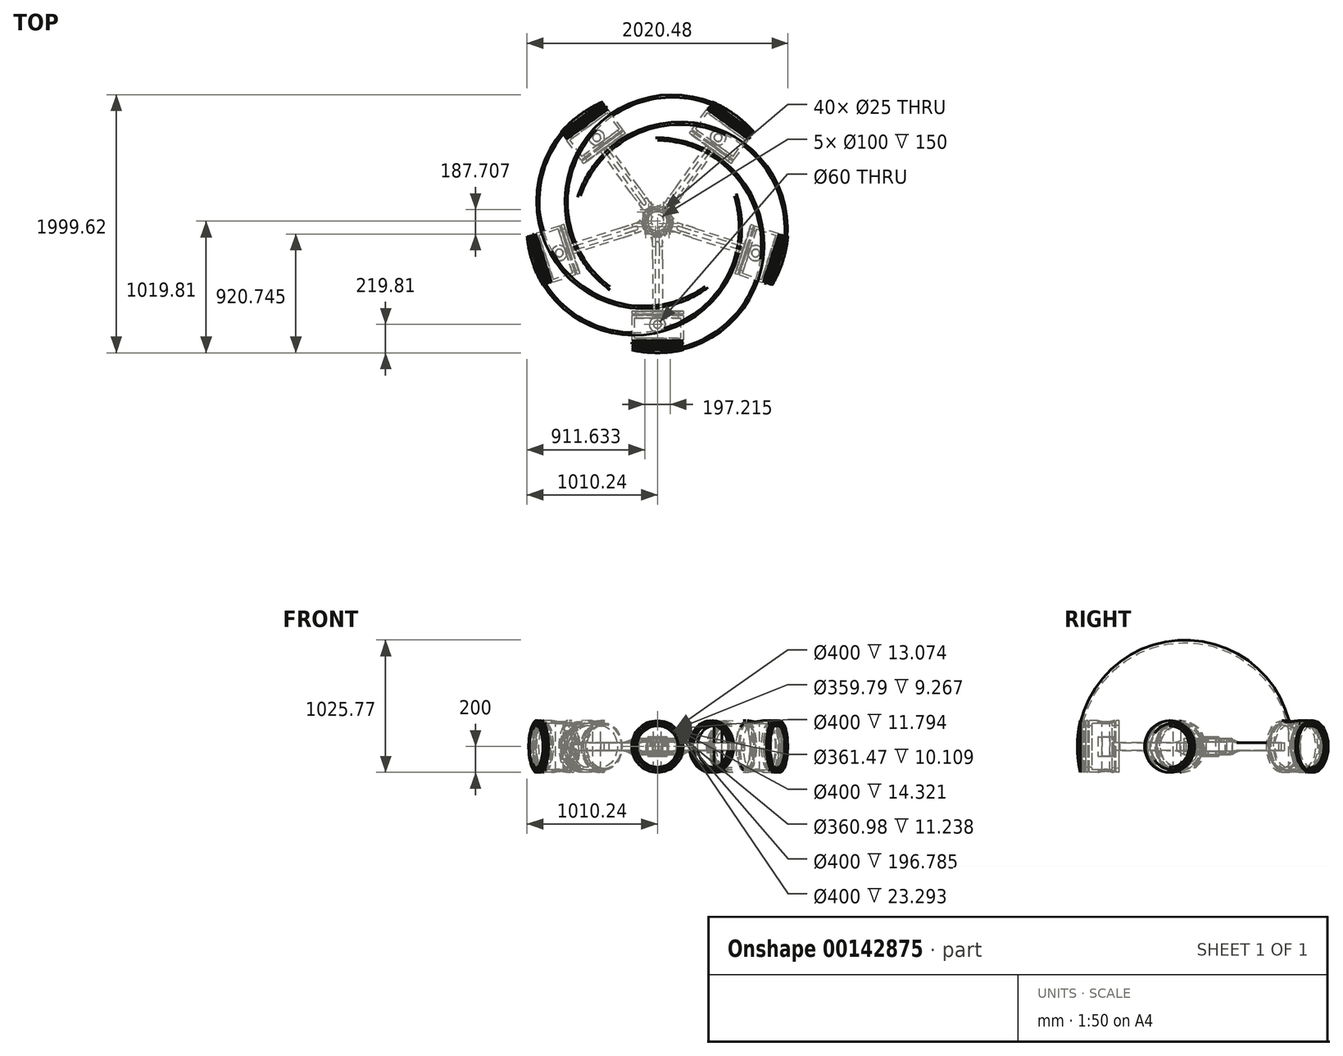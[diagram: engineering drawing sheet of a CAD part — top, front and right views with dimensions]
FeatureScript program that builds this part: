
annotation { "Feature Type Name" : "Feature", "Feature Type Description" : "" }
export const myFeature = defineFeature(function(context is Context, id is Id, definition is map)
    precondition{}
    {
        {
            var Q0;
            Q0=qCreatedBy(makeId("Top.planeOp"),FACE);
            var sketch = newSketch(context, id + "F0", { "sketchPlane" : qUnion([Q0])});
            skCircle(sketch, "E0", {"center": v(0, 0) * mm, "radius": 75 * mm});
            skCircle(sketch, "E1", {"center": v(0, 0) * mm, "radius": 50 * mm});
            skSolve(sketch);
        }
        {
            var Q0;
            Q0 = qSketchRegion(id + "F0", true);
            extrude(context, id + "F1", {"entities" : qUnion([Q0]), "endBound" : BoundingType.SYMMETRIC, "depth" : 150 * mm});
        }
        {
            var Q0;
            Q0=makeQuery(id+"F1.opExtrude","CAP_FACE",FACE,{"disambiguationData":[OSD([sQuery(id+"F0.wireOp",EDGE,"E0"),sQuery(id+"F0.wireOp",EDGE,"E1")])],"isStart":false});
            cPlane(context, id + "F2", {"entities" : qUnion([Q0]), "cplaneType" : CPlaneType.OFFSET, "offset" : 25 * mm, "oppositeDirection" : true, "width" : 150 * mm, "height" : 150 * mm});
        }
        {
            var Q0;
            Q0=qCreatedBy(id+"F2.planeOp",FACE);
            var sketch = newSketch(context, id + "F3", { "sketchPlane" : qUnion([Q0])});
            skArc(sketch, "E2", {"start": v(-113.38, -34.72) * mm, "mid": v(-113.54, -52) * mm, "end": v(-102.46, -65.26) * mm});
            skCircle(sketch, "E3", {"center": v(0, 0) * mm, "radius": 100 * mm, "construction": true});
            skArc(sketch, "E4", {"start": v(-64.07, 95.7) * mm, "mid": v(-85.62, 90.93) * mm, "end": v(-95, 70.96) * mm});
            skArc(sketch, "E5", {"start": v(93.06, 61.75) * mm, "mid": v(89.01, 87.65) * mm, "end": v(64.07, 95.7) * mm});
            skArc(sketch, "E6", {"start": v(102.46, -65.26) * mm, "mid": v(114.7, -47.42) * mm, "end": v(108.44, -26.7) * mm});
            skArc(sketch, "E7", {"start": v(-113.38, -34.72) * mm, "mid": v(-99.14, 17.24) * mm, "end": v(-95, 70.96) * mm});
            skArc(sketch, "E8", {"start": v(-64.07, 95.7) * mm, "mid": v(0, 88) * mm, "end": v(64.07, 95.7) * mm});
            skArc(sketch, "E9", {"start": v(93.06, 61.75) * mm, "mid": v(87.81, 15.27) * mm, "end": v(108.44, -26.7) * mm});
            skArc(sketch, "E10", {"start": v(-38.42, -195.41) * mm, "mid": v(-50.6, -120.58) * mm, "end": v(-102.46, -65.26) * mm});
            skArc(sketch, "E11.MirrorCS", {"start": v(38.42, -195.41) * mm, "mid": v(50.6, -120.58) * mm, "end": v(102.46, -65.26) * mm});
            skLineSegment(sketch, "E12", {"start": v(-38.42, -195.41) * mm, "end": v(38.42, -195.41) * mm});
            skCircle(sketch, "E13.0", {"center": v(0, 0) * mm, "radius": 75 * mm});
            skSolve(sketch);
        }
        {
            var Q0;
            Q0 = qSketchRegion(id + "F3", true);
            extrude(context, id + "F4", {"entities" : qUnion([Q0]), "endBound" : BoundingType.SYMMETRIC, "depth" : 25 * mm});
        }
        {
            var Q0;
            Q0=makeQuery(id+"F4.opExtrude","SWEPT_BODY",BODY,{"disambiguationData":[OSD([sQuery(id+"F3.wireOp",EDGE,"E2"),sQuery(id+"F3.wireOp",EDGE,"E4"),sQuery(id+"F3.wireOp",EDGE,"E5"),sQuery(id+"F3.wireOp",EDGE,"E6"),sQuery(id+"F3.wireOp",EDGE,"E7"),sQuery(id+"F3.wireOp",EDGE,"E8"),sQuery(id+"F3.wireOp",EDGE,"E9"),sQuery(id+"F3.wireOp",EDGE,"E10"),sQuery(id+"F3.wireOp",EDGE,"E11.MirrorCS"),sQuery(id+"F3.wireOp",EDGE,"E12")])]});
            var Q1;
            Q1=qCreatedBy(makeId("Top.planeOp"),FACE);
            mirror(context, id + "F5", {"operationType" : NewBodyOperationType.ADD, "entities" : qUnion([Q0]), "mirrorPlane" : qUnion([Q1])});
        }
        {
            var Q0;
            Q0=makeQuery(id+"F5.opPattern","COPY",FACE,{"derivedFrom":makeQuery(id+"F4.opExtrude","CAP_FACE",FACE,{"disambiguationData":[OSD([sQuery(id+"F3.wireOp",EDGE,"E2"),sQuery(id+"F3.wireOp",EDGE,"E4"),sQuery(id+"F3.wireOp",EDGE,"E5"),sQuery(id+"F3.wireOp",EDGE,"E6"),sQuery(id+"F3.wireOp",EDGE,"E7"),sQuery(id+"F3.wireOp",EDGE,"E8"),sQuery(id+"F3.wireOp",EDGE,"E9"),sQuery(id+"F3.wireOp",EDGE,"E10"),sQuery(id+"F3.wireOp",EDGE,"E11.MirrorCS"),sQuery(id+"F3.wireOp",EDGE,"E12"),sQuery(id+"F3.wireOp",EDGE,"E13.0")])],"isStart":true}),"instanceName":"1"});
            var sketch = newSketch(context, id + "F6", { "sketchPlane" : qUnion([Q0])});
            skArc(sketch, "E14", {"start": v(-38.42, -195.41) * mm, "mid": v(-40, -112.86) * mm, "end": v(-66.5, -34.67) * mm});
            skArc(sketch, "E15.MirrorCS", {"start": v(38.42, -195.41) * mm, "mid": v(40, -112.86) * mm, "end": v(66.5, -34.67) * mm});
            skArc(sketch, "E16.0", {"start": v(-66.5, -34.67) * mm, "mid": v(0, -75) * mm, "end": v(66.5, -34.67) * mm});
            skLineSegment(sketch, "E17.0", {"start": v(-38.42, -195.41) * mm, "end": v(38.42, -195.41) * mm});
            skSolve(sketch);
        }
        {
            var Q0;
            Q0 = qSketchRegion(id + "F6", true);
            extrude(context, id + "F7", {"entities" : qUnion([Q0]), "operationType" : NewBodyOperationType.ADD, "endBound" : BoundingType.UP_TO_NEXT, "depth" : 25 * mm});
        }
        {
            var Q0;
            Q0=qCreatedBy(makeId("Right.planeOp"),FACE);
            var sketch = newSketch(context, id + "F8", { "sketchPlane" : qUnion([Q0])});
            skLineSegment(sketch, "E18.bottom", {"start": v(-295.41, 30) * mm, "end": v(-695.41, 30) * mm});
            skLineSegment(sketch, "E18.top", {"start": v(-295.41, -30) * mm, "end": v(-695.41, -30) * mm});
            skLineSegment(sketch, "E18.right", {"start": v(-695.41, 30) * mm, "end": v(-695.41, -30) * mm});
            skArc(sketch, "E19", {"start": v(-295.41, 30) * mm, "mid": v(-242.84, 38.33) * mm, "end": v(-195.41, 62.5) * mm});
            skArc(sketch, "E20.MirrorCS", {"start": v(-295.41, -30) * mm, "mid": v(-242.84, -38.33) * mm, "end": v(-195.41, -62.5) * mm});
            skLineSegment(sketch, "E21.0", {"start": v(-195.41, 37.5) * mm, "end": v(-195.41, -37.5) * mm});
            skLineSegment(sketch, "E22.0", {"start": v(-195.41, 62.5) * mm, "end": v(-195.41, 37.5) * mm});
            skLineSegment(sketch, "E23.0.3", {"start": v(-195.41, -62.5) * mm, "end": v(-195.41, -37.5) * mm});
            skPoint(sketch, "E23.0.1.end.orphan", {"position": v(-65.26, -62.5) * mm});
            skPoint(sketch, "E23.0.1.start.orphan", {"position": v(-65.26, -37.5) * mm});
            skSolve(sketch);
        }
        {
            var Q0;
            Q0 = qSketchRegion(id + "F8", true);
            extrude(context, id + "F9", {"entities" : qUnion([Q0]), "operationType" : NewBodyOperationType.ADD, "endBound" : BoundingType.SYMMETRIC, "depth" : 77 * mm});
        }
        {
            var Q0;
            Q0=qCreatedBy(makeId("Top.planeOp"),FACE);
            var sketch = newSketch(context, id + "F10", { "sketchPlane" : qUnion([Q0])});
            skCircle(sketch, "E24", {"center": v(0, -800) * mm, "radius": 60 * mm});
            skCircle(sketch, "E25", {"center": v(0, -800) * mm, "radius": 30 * mm});
            skSolve(sketch);
        }
        {
            var Q0;
            Q0 = qSketchRegion(id + "F10", true);
            extrude(context, id + "F11", {"entities" : qUnion([Q0]), "endBound" : BoundingType.SYMMETRIC, "depth" : 150 * mm});
        }
        {
            var Q0;
            Q0=qCreatedBy(makeId("Top.planeOp"),FACE);
            var sketch = newSketch(context, id + "F12", { "sketchPlane" : qUnion([Q0])});
            skArc(sketch, "E26.0", {"start": v(38.5, -753.98) * mm, "mid": v(0, -740) * mm, "end": v(-38.5, -753.98) * mm});
            skLineSegment(sketch, "E27", {"start": v(38.5, -695.41) * mm, "end": v(38.5, -753.98) * mm});
            skLineSegment(sketch, "E28", {"start": v(-38.5, -695.41) * mm, "end": v(-38.5, -753.98) * mm});
            skLineSegment(sketch, "E29", {"start": v(38.5, -695.41) * mm, "end": v(-38.5, -695.41) * mm});
            skPoint(sketch, "E30.0.start.orphan", {"position": v(38.5, -295.41) * mm});
            skPoint(sketch, "E31.0.start.orphan", {"position": v(-38.5, -295.41) * mm});
            skSolve(sketch);
        }
        {
            var Q0;
            Q0 = qSketchRegion(id + "F12", true);
            extrude(context, id + "F13", {"entities" : qUnion([Q0]), "endBound" : BoundingType.SYMMETRIC, "depth" : 60 * mm});
        }
        {
            var Q0;
            Q0=makeQuery(id+"F4.opExtrude","CAP_FACE",FACE,{"disambiguationData":[OSD([sQuery(id+"F3.wireOp",EDGE,"E2"),sQuery(id+"F3.wireOp",EDGE,"E4"),sQuery(id+"F3.wireOp",EDGE,"E5"),sQuery(id+"F3.wireOp",EDGE,"E6"),sQuery(id+"F3.wireOp",EDGE,"E7"),sQuery(id+"F3.wireOp",EDGE,"E8"),sQuery(id+"F3.wireOp",EDGE,"E9"),sQuery(id+"F3.wireOp",EDGE,"E10"),sQuery(id+"F3.wireOp",EDGE,"E11.MirrorCS"),sQuery(id+"F3.wireOp",EDGE,"E12"),sQuery(id+"F3.wireOp",EDGE,"E13.0")])],"isStart":false});
            var sketch = newSketch(context, id + "F14", { "sketchPlane" : qUnion([Q0])});
            skCircle(sketch, "E32", {"center": v(90, -43.59) * mm, "radius": 12.5 * mm});
            skCircle(sketch, "E33", {"center": v(70, 71.41) * mm, "radius": 12.5 * mm});
            skCircle(sketch, "E34", {"center": v(-70, 71.41) * mm, "radius": 12.5 * mm});
            skCircle(sketch, "E35", {"center": v(-90, -43.59) * mm, "radius": 12.5 * mm});
            skLineSegment(sketch, "E36.left", {"start": v(15, -174.25) * mm, "end": v(15, -674.25) * mm});
            skLineSegment(sketch, "E36.right", {"start": v(-15, -174.25) * mm, "end": v(-15, -674.25) * mm});
            skArc(sketch, "E37", {"start": v(15, -174.25) * mm, "mid": v(0, -159.25) * mm, "end": v(-15, -174.25) * mm});
            skArc(sketch, "E38", {"start": v(-15, -674.25) * mm, "mid": v(0, -689.25) * mm, "end": v(15, -674.25) * mm});
            skSolve(sketch);
        }
        {
            var Q0;
            Q0 = qSketchRegion(id + "F14", true);
            var Q1;
            Q1=makeQuery(id+"F5.opPattern","COPY",FACE,{"derivedFrom":makeQuery(id+"F4.opExtrude","CAP_FACE",FACE,{"disambiguationData":[OSD([sQuery(id+"F3.wireOp",EDGE,"E2"),sQuery(id+"F3.wireOp",EDGE,"E4"),sQuery(id+"F3.wireOp",EDGE,"E5"),sQuery(id+"F3.wireOp",EDGE,"E6"),sQuery(id+"F3.wireOp",EDGE,"E7"),sQuery(id+"F3.wireOp",EDGE,"E8"),sQuery(id+"F3.wireOp",EDGE,"E9"),sQuery(id+"F3.wireOp",EDGE,"E10"),sQuery(id+"F3.wireOp",EDGE,"E11.MirrorCS"),sQuery(id+"F3.wireOp",EDGE,"E12"),sQuery(id+"F3.wireOp",EDGE,"E13.0")])],"isStart":false}),"instanceName":"1"});
            extrude(context, id + "F15", {"entities" : qUnion([Q0]), "operationType" : NewBodyOperationType.REMOVE, "endBound" : BoundingType.UP_TO_SURFACE, "oppositeDirection" : true, "endBoundEntityFace" : qUnion([Q1]), "depth" : 25 * mm});
        }
        {
            var Q0;
            Q0=qCreatedBy(makeId("Right.planeOp"),FACE);
            var sketch = newSketch(context, id + "F16", { "sketchPlane" : qUnion([Q0])});
            skLineSegment(sketch, "E39", {"start": v(-997.25, 0) * mm, "end": v(-697.25, 0) * mm});
            skLineSegment(sketch, "E40", {"start": v(-697.25, 0) * mm, "end": v(-697.25, -200) * mm});
            skLineSegment(sketch, "E41", {"start": v(-697.25, -200) * mm, "end": v(-720.54, -200) * mm});
            skLineSegment(sketch, "E42", {"start": v(-720.54, -200) * mm, "end": v(-720.54, -184.88) * mm});
            skLineSegment(sketch, "E43", {"start": v(-720.54, -184.88) * mm, "end": v(-730.66, -183.75) * mm});
            skLineSegment(sketch, "E44", {"start": v(-730.66, -183.75) * mm, "end": v(-730.66, -200) * mm});
            skLineSegment(sketch, "E45", {"start": v(-730.66, -200) * mm, "end": v(-927.45, -200) * mm});
            skLineSegment(sketch, "E46", {"start": v(-927.45, -200) * mm, "end": v(-927.45, -180.5) * mm});
            skLineSegment(sketch, "E47", {"start": v(-927.45, -180.5) * mm, "end": v(-938.68, -180.5) * mm});
            skLineSegment(sketch, "E48", {"start": v(-938.68, -180.5) * mm, "end": v(-938.68, -200) * mm});
            skLineSegment(sketch, "E49", {"start": v(-938.68, -200) * mm, "end": v(-953, -200) * mm});
            skLineSegment(sketch, "E50", {"start": v(-953, -200) * mm, "end": v(-953, -180.74) * mm});
            skLineSegment(sketch, "E51", {"start": v(-953, -180.74) * mm, "end": v(-963.11, -180.74) * mm});
            skLineSegment(sketch, "E52", {"start": v(-963.11, -180.74) * mm, "end": v(-963.11, -200) * mm});
            skLineSegment(sketch, "E53", {"start": v(-963.11, -200) * mm, "end": v(-974.9, -200) * mm});
            skLineSegment(sketch, "E54", {"start": v(-974.9, -200) * mm, "end": v(-974.9, -179.9) * mm});
            skLineSegment(sketch, "E55", {"start": v(-974.9, -179.9) * mm, "end": v(-984.18, -179.9) * mm});
            skLineSegment(sketch, "E56", {"start": v(-984.18, -179.9) * mm, "end": v(-984.18, -200) * mm});
            skLineSegment(sketch, "E57", {"start": v(-984.18, -200) * mm, "end": v(-997.25, -200) * mm});
            skLineSegment(sketch, "E58", {"start": v(-1171, 0) * mm, "end": v(-373.1, 0) * mm, "construction": true});
            skArc(sketch, "E59", {"start": v(-1019.78, 0) * mm, "mid": v(-1014.57, -100.68) * mm, "end": v(-997.25, -200) * mm});
            skLineSegment(sketch, "E60", {"start": v(-1019.78, 0) * mm, "end": v(-997.25, 0) * mm});
            skSolve(sketch);
        }
        {
            var Q0;
            Q0 = qSketchRegion(id + "F16", true);
            var Q1;
            Q1=sQuery(id+"F16.wireOp",EDGE,"E58");
            revolve(context, id + "F17", {"entities" : qUnion([Q0]), "axis" : qUnion([Q1]), "revolveType" : RevolveType.FULL});
        }
        {
            var Q0;
            Q0=qCreatedBy(makeId("Top.planeOp"),FACE);
            var sketch = newSketch(context, id + "F18", { "sketchPlane" : qUnion([Q0])});
            skCircle(sketch, "E61.0", {"center": v(0, -800) * mm, "radius": 30 * mm});
            skSolve(sketch);
        }
        {
            var Q0;
            Q0 = qSketchRegion(id + "F18", true);
            var Q1;
            Q1=makeQuery(id+"F17.opRevolve","SWEPT_FACE",FACE,{"disambiguationData":[OSD([sQuery(id+"F16.wireOp",EDGE,"E45")])]});
            extrude(context, id + "F19", {"entities" : qUnion([Q0]), "endBound" : BoundingType.SYMMETRIC, "oppositeDirection" : true, "endBoundEntityFace" : qUnion([Q1]), "depth" : 500 * mm});
        }
        {
            var Q0;
            Q0=qCreatedBy(makeId("Top.planeOp"),FACE);
            cPlane(context, id + "F20", {"entities" : qUnion([Q0]), "cplaneType" : CPlaneType.OFFSET, "offset" : 250 * mm, "width" : 150 * mm, "height" : 150 * mm});
        }
        {
            var Q0;
            Q0=qCreatedBy(id+"F20.planeOp",FACE);
            var sketch = newSketch(context, id + "F21", { "sketchPlane" : qUnion([Q0])});
            skCircle(sketch, "E62.0", {"center": v(0, -800) * mm, "radius": 60 * mm});
            skSolve(sketch);
        }
        {
            var Q0;
            Q0 = qSketchRegion(id + "F21", true);
            extrude(context, id + "F22", {"entities" : qUnion([Q0]), "oppositeDirection" : true, "depth" : 60 * mm});
        }
        {
            var Q0;
            Q0=makeQuery(id+"F22.opExtrude","SWEPT_BODY",BODY,{"disambiguationData":[OSD([sQuery(id+"F21.wireOp",EDGE,"E62.0")])]});
            var Q1;
            Q1=qCreatedBy(makeId("Top.planeOp"),FACE);
            mirror(context, id + "F23", {"entities" : qUnion([Q0]), "mirrorPlane" : qUnion([Q1])});
        }
        {
            var Q0;
            Q0=makeQuery(id+"F17.opRevolve","SWEPT_FACE",FACE,{"disambiguationData":[OSD([sQuery(id+"F16.wireOp",EDGE,"E40")])]});
            shell(context, id + "F24", {"entities" : qUnion([Q0]), "thickness" : 20 * mm});
        }
        {
            var Q0;
            Q0=makeQuery(id+"F19.opExtrude","SWEPT_BODY",BODY,{"disambiguationData":[OSD([sQuery(id+"F18.wireOp",EDGE,"E61.0")])]});
            var Q1;
            Q1=makeQuery(id+"F17.opRevolve","SWEPT_BODY",BODY,{"disambiguationData":[OSD([sQuery(id+"F16.wireOp",EDGE,"E39"),sQuery(id+"F16.wireOp",EDGE,"E40"),sQuery(id+"F16.wireOp",EDGE,"E41"),sQuery(id+"F16.wireOp",EDGE,"E42"),sQuery(id+"F16.wireOp",EDGE,"E43"),sQuery(id+"F16.wireOp",EDGE,"E44"),sQuery(id+"F16.wireOp",EDGE,"E45"),sQuery(id+"F16.wireOp",EDGE,"E46"),sQuery(id+"F16.wireOp",EDGE,"E47"),sQuery(id+"F16.wireOp",EDGE,"E48"),sQuery(id+"F16.wireOp",EDGE,"E49"),sQuery(id+"F16.wireOp",EDGE,"E50"),sQuery(id+"F16.wireOp",EDGE,"E51"),sQuery(id+"F16.wireOp",EDGE,"E52"),sQuery(id+"F16.wireOp",EDGE,"E53"),sQuery(id+"F16.wireOp",EDGE,"E54"),sQuery(id+"F16.wireOp",EDGE,"E55"),sQuery(id+"F16.wireOp",EDGE,"E56"),sQuery(id+"F16.wireOp",EDGE,"E57"),sQuery(id+"F16.wireOp",EDGE,"E59"),sQuery(id+"F16.wireOp",EDGE,"E60")])]});
            booleanBodies(context, id + "F25", {"operationType" : BooleanOperationType.SUBTRACTION, "tools" : qUnion([Q0]), "targets" : qUnion([Q1])});
        }
        {
            var Q0;
            Q0=makeQuery(id+"F22.opExtrude","SWEPT_BODY",BODY,{"disambiguationData":[OSD([sQuery(id+"F21.wireOp",EDGE,"E62.0")])]});
            var Q1;
            Q1=makeQuery(id+"F23.opPattern","COPY",BODY,{"derivedFrom":makeQuery(id+"F22.opExtrude","SWEPT_BODY",BODY,{"disambiguationData":[OSD([sQuery(id+"F21.wireOp",EDGE,"E62.0")])]}),"instanceName":"1"});
            var Q2;
            Q2=makeQuery(id+"F17.opRevolve","SWEPT_BODY",BODY,{"disambiguationData":[OSD([sQuery(id+"F16.wireOp",EDGE,"E39"),sQuery(id+"F16.wireOp",EDGE,"E40"),sQuery(id+"F16.wireOp",EDGE,"E41"),sQuery(id+"F16.wireOp",EDGE,"E42"),sQuery(id+"F16.wireOp",EDGE,"E43"),sQuery(id+"F16.wireOp",EDGE,"E44"),sQuery(id+"F16.wireOp",EDGE,"E45"),sQuery(id+"F16.wireOp",EDGE,"E46"),sQuery(id+"F16.wireOp",EDGE,"E47"),sQuery(id+"F16.wireOp",EDGE,"E48"),sQuery(id+"F16.wireOp",EDGE,"E49"),sQuery(id+"F16.wireOp",EDGE,"E50"),sQuery(id+"F16.wireOp",EDGE,"E51"),sQuery(id+"F16.wireOp",EDGE,"E52"),sQuery(id+"F16.wireOp",EDGE,"E53"),sQuery(id+"F16.wireOp",EDGE,"E54"),sQuery(id+"F16.wireOp",EDGE,"E55"),sQuery(id+"F16.wireOp",EDGE,"E56"),sQuery(id+"F16.wireOp",EDGE,"E57"),sQuery(id+"F16.wireOp",EDGE,"E59"),sQuery(id+"F16.wireOp",EDGE,"E60")])]});
            booleanBodies(context, id + "F26", {"operationType" : BooleanOperationType.SUBTRACTION, "tools" : qUnion([Q0, Q1]), "targets" : qUnion([Q2])});
        }
        {
            var Q0;
            Q0=makeQuery(id+"F26.opBoolean","COPY",FACE,{"derivedFrom":makeQuery(id+"F22.opExtrude","CAP_FACE",FACE,{"disambiguationData":[OSD([sQuery(id+"F21.wireOp",EDGE,"E62.0")])],"isStart":false})});
            var sketch = newSketch(context, id + "F27", { "sketchPlane" : qUnion([Q0])});
            skCircle(sketch, "E63.0", {"center": v(0, -800) * mm, "radius": 30 * mm});
            skSolve(sketch);
        }
        {
            var Q0;
            Q0 = qSketchRegion(id + "F27", true);
            var Q1;
            Q1=makeQuery(id+"F26.opBoolean","COPY",FACE,{"derivedFrom":makeQuery(id+"F23.opPattern","COPY",FACE,{"derivedFrom":makeQuery(id+"F22.opExtrude","CAP_FACE",FACE,{"disambiguationData":[OSD([sQuery(id+"F21.wireOp",EDGE,"E62.0")])],"isStart":false}),"instanceName":"1"})});
            extrude(context, id + "F28", {"entities" : qUnion([Q0]), "endBound" : BoundingType.UP_TO_SURFACE, "oppositeDirection" : true, "endBoundEntityFace" : qUnion([Q1]), "depth" : 25 * mm});
        }
        {
            var Q0;
            Q0=qCreatedBy(makeId("Right.planeOp"),FACE);
            var sketch = newSketch(context, id + "F29", { "sketchPlane" : qUnion([Q0])});
            skLineSegment(sketch, "E64", {"start": v(0, 170.83) * mm, "end": v(0, -212.59) * mm, "construction": true});
            skSolve(sketch);
        }
        {
            var Q0;
            Q0=makeQuery(id+"F1.opExtrude","SWEPT_BODY",BODY,{"disambiguationData":[OSD([sQuery(id+"F0.wireOp",EDGE,"E0"),sQuery(id+"F0.wireOp",EDGE,"E1")])]});
            var Q1;
            Q1=makeQuery(id+"F17.opRevolve","SWEPT_BODY",BODY,{"disambiguationData":[OSD([sQuery(id+"F16.wireOp",EDGE,"E39"),sQuery(id+"F16.wireOp",EDGE,"E40"),sQuery(id+"F16.wireOp",EDGE,"E41"),sQuery(id+"F16.wireOp",EDGE,"E42"),sQuery(id+"F16.wireOp",EDGE,"E43"),sQuery(id+"F16.wireOp",EDGE,"E44"),sQuery(id+"F16.wireOp",EDGE,"E45"),sQuery(id+"F16.wireOp",EDGE,"E46"),sQuery(id+"F16.wireOp",EDGE,"E47"),sQuery(id+"F16.wireOp",EDGE,"E48"),sQuery(id+"F16.wireOp",EDGE,"E49"),sQuery(id+"F16.wireOp",EDGE,"E50"),sQuery(id+"F16.wireOp",EDGE,"E51"),sQuery(id+"F16.wireOp",EDGE,"E52"),sQuery(id+"F16.wireOp",EDGE,"E53"),sQuery(id+"F16.wireOp",EDGE,"E54"),sQuery(id+"F16.wireOp",EDGE,"E55"),sQuery(id+"F16.wireOp",EDGE,"E56"),sQuery(id+"F16.wireOp",EDGE,"E57"),sQuery(id+"F16.wireOp",EDGE,"E59"),sQuery(id+"F16.wireOp",EDGE,"E60")])]});
            var Q2;
            Q2=makeQuery(id+"F28.opExtrude","SWEPT_BODY",BODY,{"disambiguationData":[OSD([sQuery(id+"F27.wireOp",EDGE,"E63.0")])]});
            var Q3;
            Q3=sQuery(id+"F29.wireOp",EDGE,"E64");
            circularPattern(context, id + "F30", {"entities" : qUnion([Q0, Q1, Q2]), "axis" : qUnion([Q3]), "angle" : 72 * degree, "instanceCount" : 5});
        }
    });
